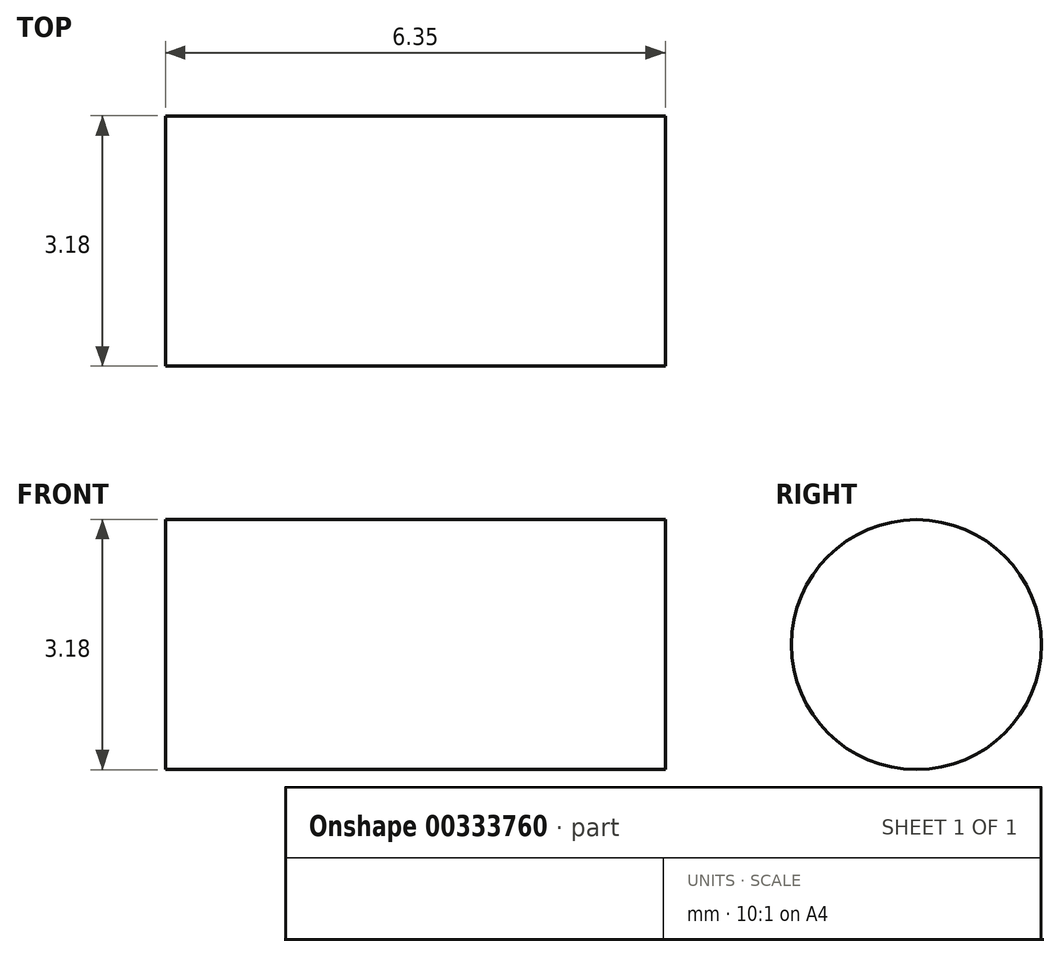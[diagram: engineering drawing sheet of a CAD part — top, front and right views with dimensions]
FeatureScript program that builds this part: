
annotation { "Feature Type Name" : "Feature", "Feature Type Description" : "" }
export const myFeature = defineFeature(function(context is Context, id is Id, definition is map)
    precondition{}
    {
        {
            var Q0;
            Q0=qCreatedBy(makeId("Right.planeOp"),FACE);
            var sketch = newSketch(context, id + "F0", { "sketchPlane" : qUnion([Q0])});
            skCircle(sketch, "E0", {"center": v(0, 0) * mm, "radius": 1.59 * mm});
            skSolve(sketch);
        }
        {
            var Q0;
            Q0 = qSketchRegion(id + "F0", true);
            extrude(context, id + "F1", {"entities" : qUnion([Q0]), "depth" : 6.35 * mm});
        }
    });
